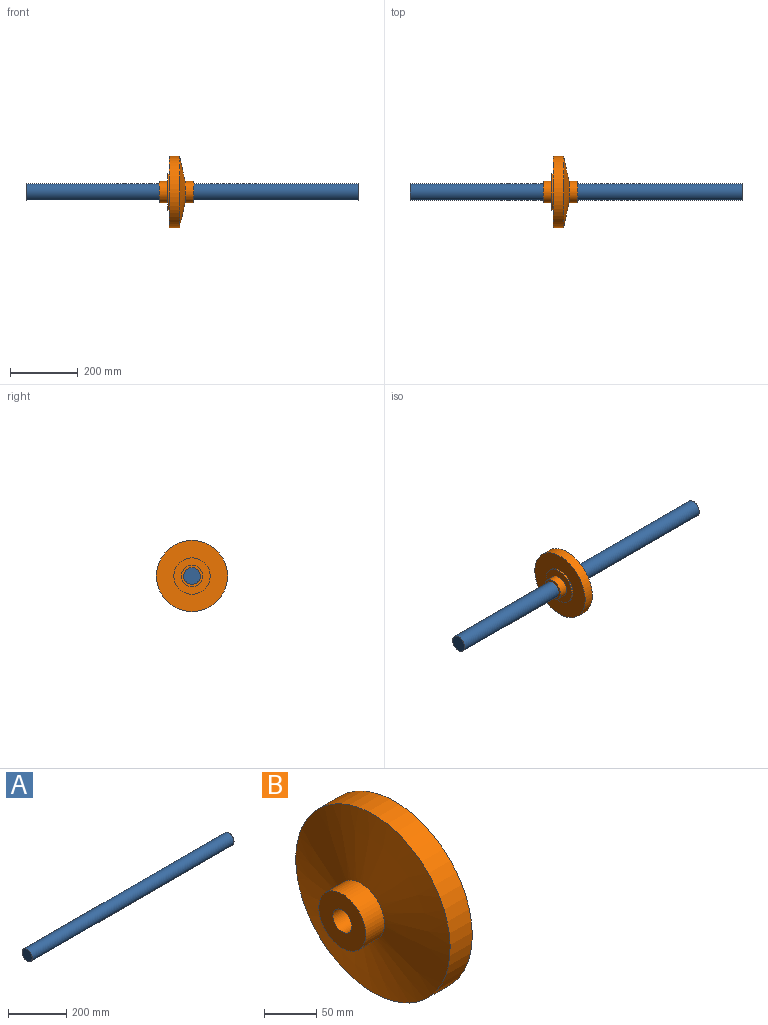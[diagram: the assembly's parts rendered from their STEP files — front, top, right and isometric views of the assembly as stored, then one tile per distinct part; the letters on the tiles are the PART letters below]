
ASSEMBLY  parts=2 mates=1
PART A: 3 faces, bbox 977.9x49.2x49.2 mm
  f0: plane 49.17x49.17mm, normal (-1,0,0), area 1899.2mm2, adj f2
  f1: plane 49.17x49.17mm, normal (1,0,0), area 1899.2mm2, adj f2
  f2: cylinder r=24.59mm len=977.9mm, axis (-1,0,0), area 151071.8mm2, adj f0,f1
PART B: 10 faces, bbox 101.6x209.6x209.6 mm
  f0: cylinder r=104.77mm len=209.55mm, axis (1,0,0), area 19748.5mm2, adj f1,f9
  f1: cone r=104.77mm half-angle=77.5deg, axis (1,0,0), area 32082.6mm2, adj f0,f2
  f2: cylinder r=31.75mm len=63.5mm, axis (1,0,0), area 5067.1mm2, adj f1,f3
  f3: plane 63.5x63.5mm, normal (-1,0,0), area 2660.2mm2, adj f2,f4
  f4: cylinder r=12.7mm len=101.6mm, axis (1,0,0), area 8107.3mm2, adj f3,f5
  f5: plane 63.5x63.5mm, normal (1,0,0), area 2660.2mm2, adj f4,f6
  f6: cylinder r=31.75mm len=63.5mm, axis (1,0,0), area 5067.1mm2, adj f5,f7
  f7: plane 106.95x106.95mm, normal (1,0,0), area 5817.4mm2, adj f6,f8
  f8: cylinder r=53.48mm len=106.95mm, axis (1,0,0), area 1545mm2, adj f7,f9
  f9: plane 209.55x209.55mm, normal (1,0,0), area 25503.5mm2, adj f0,f8
PLACE A t=(-181,11.93,-87.61)mm
PLACE B rot(axis=(0,1,0),180deg) t=(55.15,11.93,-87.61)mm
MATE planar B.f0 <-> A.f2  axis (-1,0,0) through (55.15,11.93,-87.61)mm
